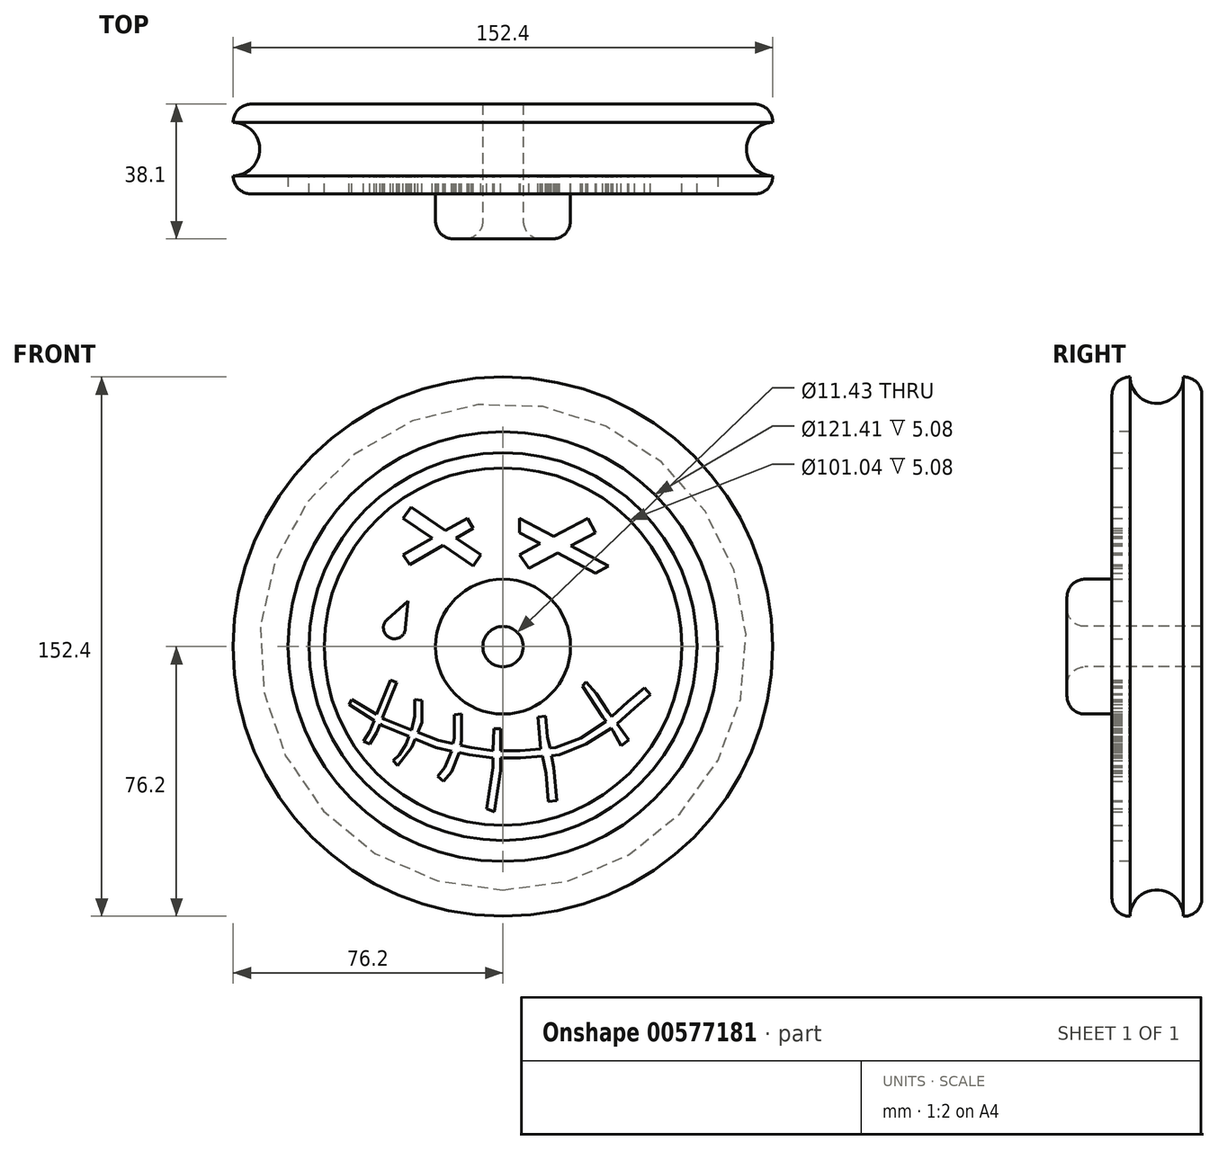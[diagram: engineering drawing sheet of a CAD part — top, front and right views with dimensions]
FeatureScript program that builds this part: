
annotation { "Feature Type Name" : "Feature", "Feature Type Description" : "" }
export const myFeature = defineFeature(function(context is Context, id is Id, definition is map)
    precondition{}
    {
        {
            var Q0;
            Q0=qCreatedBy(makeId("Front.planeOp"),FACE);
            var sketch = newSketch(context, id + "F0", { "sketchPlane" : qUnion([Q0])});
            skCircle(sketch, "E0", {"center": v(0, 0) * mm, "radius": 76.2 * mm});
            skSolve(sketch);
        }
        {
            var Q0;
            Q0=makeQuery(id+"F0.imprint","IMPRINT",FACE,{"disambiguationData":[TD([[makeQuery(id+"F0.imprint","IMPRINT",EDGE,{"derivedFrom":sQuery(id+"F0.wireOp",EDGE,"E0")}),1.0]])]});
            extrude(context, id + "F1", {"entities" : qUnion([Q0]), "depth" : 25.4 * mm, "offsetDistance" : 25.4 * mm, "symmetric" : true});
        }
        {
            var Q0;
            Q0=makeQuery(id+"F1.opExtrude","CAP_FACE",FACE,{"disambiguationData":[OSD([sQuery(id+"F0.wireOp",EDGE,"E0")])],"isStart":false});
            var sketch = newSketch(context, id + "F2", { "sketchPlane" : qUnion([Q0])});
            skCircle(sketch, "E1", {"center": v(0, 0) * mm, "radius": 19.05 * mm});
            skSolve(sketch);
        }
        {
            var Q0;
            Q0=makeQuery(id+"F2.imprint","IMPRINT",FACE,{"disambiguationData":[TD([[makeQuery(id+"F2.imprint","IMPRINT",EDGE,{"derivedFrom":sQuery(id+"F2.wireOp",EDGE,"E1")}),1.0]])]});
            extrude(context, id + "F3", {"entities" : qUnion([Q0]), "operationType" : NewBodyOperationType.ADD, "depth" : 12.7 * mm, "offsetDistance" : 25.4 * mm});
        }
        {
            var Q0;
            Q0=makeQuery(id+"F3.opExtrude","CAP_FACE",FACE,{"disambiguationData":[OSD([sQuery(id+"F2.wireOp",EDGE,"E1")])],"isStart":false});
            var sketch = newSketch(context, id + "F4", { "sketchPlane" : qUnion([Q0])});
            skCircle(sketch, "E2", {"center": v(0, 0) * mm, "radius": 5.72 * mm});
            skSolve(sketch);
        }
        {
            var Q0;
            Q0=sQuery(id+"F4.wireOp",VERTEX,"E2.center");
            var Q1;
            Q1=makeQuery(id+"F1.opExtrude","SWEPT_BODY",BODY,{"disambiguationData":[OSD([sQuery(id+"F0.wireOp",EDGE,"E0")])]});
            hole(context, id + "F5", {"style" : HoleStyle.SIMPLE, "endStyle" : HoleEndStyle.THROUGH, "holeDiameter" : 11.43 * mm, "isTappedThrough" : true, "tappedDepth" : 12.7 * mm, "tapClearance" : 3, "locations" : qUnion([Q0]), "scope" : qUnion([Q1])});
        }
        {
            var Q0;
            Q0=makeQuery(id+"F1.opExtrude","CAP_EDGE",EDGE,{"disambiguationData":[OSD([sQuery(id+"F0.wireOp",EDGE,"E0")])],"isStart":false});
            var Q1;
            Q1=makeQuery(id+"F1.opExtrude","SWEPT_FACE",FACE,{"disambiguationData":[OSD([sQuery(id+"F0.wireOp",EDGE,"E0")])]});
            var Q2;
            Q2=makeQuery(id+"F3.opExtrude","CAP_FACE",FACE,{"disambiguationData":[OSD([sQuery(id+"F2.wireOp",EDGE,"E1")])],"isStart":false});
            fillet(context, id + "F6", {"entities" : qUnion([Q0, Q1, Q2]), "radius" : 5.08 * mm, "tangentPropagation" : true, "allowEdgeOverflow" : false});
        }
        {
            var Q0;
            Q0=makeQuery(id+"F1.opExtrude","CAP_FACE",FACE,{"disambiguationData":[OSD([sQuery(id+"F0.wireOp",EDGE,"E0")])],"isStart":false});
            var sketch = newSketch(context, id + "F7", { "sketchPlane" : qUnion([Q0])});
            skCircle(sketch, "E3", {"center": v(0, 0) * mm, "radius": 60.7 * mm});
            skSolve(sketch);
        }
        {
            var Q0;
            Q0=makeQuery(id+"F7.imprint","IMPRINT",FACE,{"disambiguationData":[TD([[makeQuery(id+"F7.imprint","IMPRINT",EDGE,{"derivedFrom":sQuery(id+"F7.wireOp",EDGE,"E3")}),1.0]])]});
            extrude(context, id + "F8", {"entities" : qUnion([Q0]), "operationType" : NewBodyOperationType.REMOVE, "oppositeDirection" : true, "depth" : 5.08 * mm, "offsetDistance" : 25.4 * mm});
        }
        {
            var Q0;
            Q0=makeQuery(id+"F8.boolean.opBoolean","COPY",FACE,{"derivedFrom":makeQuery(id+"F8.opExtrude","CAP_FACE",FACE,{"disambiguationData":[OSD([sQuery(id+"F2.wireOp",EDGE,"E1"),sQuery(id+"F7.wireOp",EDGE,"E3")])],"isStart":false})});
            var sketch = newSketch(context, id + "F9", { "sketchPlane" : qUnion([Q0])});
            skCircle(sketch, "E4", {"center": v(0, 0) * mm, "radius": 54.78 * mm});
            skCircle(sketch, "E5", {"center": v(0, 0) * mm, "radius": 50.52 * mm});
            skSolve(sketch);
        }
        {
            var Q0;
            Q0=makeQuery(id+"F9.imprint","IMPRINT",FACE,{"disambiguationData":[TD([[makeQuery(id+"F9.imprint","IMPRINT",EDGE,{"derivedFrom":sQuery(id+"F9.wireOp",EDGE,"E5")}),1.0]])]});
            var sketch = newSketch(context, id + "F10", { "sketchPlane" : qUnion([Q0])});
            skLineSegment(sketch, "E6", {"start": v(-28.19, 25.94) * mm, "end": v(-10.05, 36.3) * mm});
            skLineSegment(sketch, "E7", {"start": v(-10.05, 36.3) * mm, "end": v(-8.42, 33.43) * mm});
            skLineSegment(sketch, "E8", {"start": v(-8.42, 33.43) * mm, "end": v(-26.29, 23.22) * mm});
            skLineSegment(sketch, "E9", {"start": v(-26.29, 23.22) * mm, "end": v(-28.19, 25.94) * mm});
            skLineSegment(sketch, "E10", {"start": v(-28.19, 36.3) * mm, "end": v(-8.42, 22.78) * mm});
            skLineSegment(sketch, "E11", {"start": v(-8.42, 22.78) * mm, "end": v(-6.26, 25.94) * mm});
            skLineSegment(sketch, "E12", {"start": v(-6.26, 25.94) * mm, "end": v(-25.93, 39.4) * mm});
            skLineSegment(sketch, "E13", {"start": v(-25.93, 39.4) * mm, "end": v(-28.19, 36.3) * mm});
            skLineSegment(sketch, "E14", {"start": v(4.65, 25.95) * mm, "end": v(23.96, 36.3) * mm});
            skLineSegment(sketch, "E15", {"start": v(23.96, 36.3) * mm, "end": v(26.15, 32.23) * mm});
            skLineSegment(sketch, "E16", {"start": v(26.15, 32.23) * mm, "end": v(7.28, 22.12) * mm});
            skLineSegment(sketch, "E17", {"start": v(7.28, 22.12) * mm, "end": v(4.65, 25.95) * mm});
            skLineSegment(sketch, "E18", {"start": v(4.65, 36.3) * mm, "end": v(29.75, 22.73) * mm});
            skLineSegment(sketch, "E19", {"start": v(29.75, 22.73) * mm, "end": v(26.15, 20.8) * mm});
            skLineSegment(sketch, "E20", {"start": v(26.15, 20.8) * mm, "end": v(4.65, 32.23) * mm});
            skLineSegment(sketch, "E21", {"start": v(4.65, 32.23) * mm, "end": v(4.65, 36.3) * mm});
            skSolve(sketch);
        }
        {
            var Q0;
            Q0 = qSketchRegion(id + "F10", true);
            extrude(context, id + "F11", {"entities" : qUnion([Q0]), "operationType" : NewBodyOperationType.ADD, "depth" : 5.08 * mm, "offsetDistance" : 25.4 * mm});
        }
        {
            var Q0;
            Q0=makeQuery(id+"F9.imprint","IMPRINT",FACE,{"disambiguationData":[TD([[makeQuery(id+"F9.imprint","IMPRINT",EDGE,{"derivedFrom":sQuery(id+"F9.wireOp",EDGE,"E4")}),1.0]])]});
            extrude(context, id + "F12", {"entities" : qUnion([Q0]), "operationType" : NewBodyOperationType.ADD, "depth" : 5.08 * mm, "offsetDistance" : 25.4 * mm});
        }
        {
            var Q0;
            {var subQ4=sQuery(id+"F2.wireOp",EDGE,"E1");Q0=makeQuery(id+"F12.boolean.opBoolean","SPLIT",FACE,{"disambiguationData":[TD([makeQuery(id+"F3.opExtrude","SWEPT_FACE",FACE,{"disambiguationData":[OSD([subQ4])]})])],"derivedFrom":makeQuery(id+"F8.boolean.opBoolean","COPY",FACE,{"derivedFrom":makeQuery(id+"F8.opExtrude","CAP_FACE",FACE,{"disambiguationData":[OSD([subQ4,sQuery(id+"F7.wireOp",EDGE,"E3")])],"isStart":false})})});}
            var sketch = newSketch(context, id + "F13", { "sketchPlane" : qUnion([Q0])});
            skLineSegment(sketch, "E22", {"start": v(-42.77, -14.96) * mm, "end": v(-33.4, -20.53) * mm});
            skLineSegment(sketch, "E23", {"start": v(-33.4, -20.53) * mm, "end": v(-18.23, -26.56) * mm});
            skLineSegment(sketch, "E24", {"start": v(-18.23, -26.56) * mm, "end": v(-8.86, -28.57) * mm});
            skLineSegment(sketch, "E25", {"start": v(-8.86, -28.57) * mm, "end": v(-2.84, -29.46) * mm});
            skLineSegment(sketch, "E26", {"start": v(-2.84, -29.46) * mm, "end": v(4.75, -29.46) * mm});
            skLineSegment(sketch, "E27", {"start": v(4.75, -29.46) * mm, "end": v(14.79, -28.57) * mm});
            skLineSegment(sketch, "E28", {"start": v(14.79, -28.57) * mm, "end": v(21.92, -25.89) * mm});
            skLineSegment(sketch, "E29", {"start": v(21.92, -25.89) * mm, "end": v(29.06, -21.2) * mm});
            skLineSegment(sketch, "E30", {"start": v(29.06, -21.2) * mm, "end": v(35.31, -15.63) * mm});
            skLineSegment(sketch, "E31", {"start": v(35.31, -15.63) * mm, "end": v(40, -11.61) * mm});
            skLineSegment(sketch, "E32", {"start": v(40, -11.61) * mm, "end": v(41.62, -13.5) * mm});
            skLineSegment(sketch, "E33", {"start": v(41.62, -13.5) * mm, "end": v(37.12, -17.36) * mm});
            skLineSegment(sketch, "E34", {"start": v(37.12, -17.36) * mm, "end": v(31.07, -22.76) * mm});
            skLineSegment(sketch, "E35", {"start": v(31.07, -22.76) * mm, "end": v(23.49, -27.45) * mm});
            skLineSegment(sketch, "E36", {"start": v(23.49, -27.45) * mm, "end": v(15.9, -30.57) * mm});
            skLineSegment(sketch, "E37", {"start": v(15.9, -30.57) * mm, "end": v(4.97, -31.47) * mm});
            skLineSegment(sketch, "E38", {"start": v(4.97, -31.47) * mm, "end": v(-2.4, -31.47) * mm});
            skLineSegment(sketch, "E39", {"start": v(-2.4, -31.47) * mm, "end": v(-9.53, -30.57) * mm});
            skLineSegment(sketch, "E40", {"start": v(-9.53, -30.57) * mm, "end": v(-18.9, -28.57) * mm});
            skLineSegment(sketch, "E41", {"start": v(-18.9, -28.57) * mm, "end": v(-34.07, -22.32) * mm});
            skLineSegment(sketch, "E42", {"start": v(-34.07, -22.32) * mm, "end": v(-43.44, -16.3) * mm});
            skLineSegment(sketch, "E43", {"start": v(-43.44, -16.3) * mm, "end": v(-42.77, -14.96) * mm});
            skLineSegment(sketch, "E44", {"start": v(-30.05, -10.05) * mm, "end": v(-35.74, -24.37) * mm});
            skLineSegment(sketch, "E45", {"start": v(-35.74, -24.37) * mm, "end": v(-37.57, -27.45) * mm});
            skLineSegment(sketch, "E46", {"start": v(-37.57, -27.45) * mm, "end": v(-39.36, -26.74) * mm});
            skLineSegment(sketch, "E47", {"start": v(-39.36, -26.74) * mm, "end": v(-37.57, -23.96) * mm});
            skLineSegment(sketch, "E48", {"start": v(-37.57, -23.96) * mm, "end": v(-31.82, -9.47) * mm});
            skLineSegment(sketch, "E49", {"start": v(-31.82, -9.47) * mm, "end": v(-30.05, -10.05) * mm});
            skLineSegment(sketch, "E50", {"start": v(-24.92, -14.96) * mm, "end": v(-24.92, -17.36) * mm});
            skLineSegment(sketch, "E51", {"start": v(-24.92, -17.36) * mm, "end": v(-24.92, -19.64) * mm});
            skLineSegment(sketch, "E52", {"start": v(-24.92, -19.64) * mm, "end": v(-25.82, -23.55) * mm});
            skLineSegment(sketch, "E53", {"start": v(-25.82, -23.55) * mm, "end": v(-27.37, -27.45) * mm});
            skLineSegment(sketch, "E54", {"start": v(-27.37, -27.45) * mm, "end": v(-29.23, -30.57) * mm});
            skLineSegment(sketch, "E55", {"start": v(-29.23, -30.57) * mm, "end": v(-31.08, -32.23) * mm});
            skLineSegment(sketch, "E56", {"start": v(-31.08, -32.23) * mm, "end": v(-29.81, -33.66) * mm});
            skLineSegment(sketch, "E57", {"start": v(-29.81, -33.66) * mm, "end": v(-25.82, -28.57) * mm});
            skLineSegment(sketch, "E58", {"start": v(-25.82, -28.57) * mm, "end": v(-24.81, -26.13) * mm});
            skLineSegment(sketch, "E59", {"start": v(-24.81, -26.13) * mm, "end": v(-24.06, -24.24) * mm});
            skLineSegment(sketch, "E60", {"start": v(-24.06, -24.24) * mm, "end": v(-22.96, -21.45) * mm});
            skLineSegment(sketch, "E61", {"start": v(-22.96, -21.45) * mm, "end": v(-22.96, -18.3) * mm});
            skLineSegment(sketch, "E62", {"start": v(-22.96, -18.3) * mm, "end": v(-22.96, -15.18) * mm});
            skLineSegment(sketch, "E63", {"start": v(-22.96, -15.18) * mm, "end": v(-24.92, -14.96) * mm});
            skLineSegment(sketch, "E64", {"start": v(-13.77, -19.2) * mm, "end": v(-13.77, -23.66) * mm});
            skLineSegment(sketch, "E65", {"start": v(-13.77, -23.66) * mm, "end": v(-13.77, -25.89) * mm});
            skLineSegment(sketch, "E66", {"start": v(-13.77, -25.89) * mm, "end": v(-14.54, -29.5) * mm});
            skLineSegment(sketch, "E67", {"start": v(-14.54, -29.5) * mm, "end": v(-16.38, -34.12) * mm});
            skLineSegment(sketch, "E68", {"start": v(-16.38, -34.12) * mm, "end": v(-18.45, -36.6) * mm});
            skLineSegment(sketch, "E69", {"start": v(-18.45, -36.6) * mm, "end": v(-16.77, -38.01) * mm});
            skLineSegment(sketch, "E70", {"start": v(-16.77, -38.01) * mm, "end": v(-14.58, -35.4) * mm});
            skLineSegment(sketch, "E71", {"start": v(-14.58, -35.4) * mm, "end": v(-12.42, -29.95) * mm});
            skLineSegment(sketch, "E72", {"start": v(-12.42, -29.95) * mm, "end": v(-11.69, -26.56) * mm});
            skLineSegment(sketch, "E73", {"start": v(-11.69, -26.56) * mm, "end": v(-11.69, -22.54) * mm});
            skLineSegment(sketch, "E74", {"start": v(-11.69, -22.54) * mm, "end": v(-11.69, -18.97) * mm});
            skLineSegment(sketch, "E75", {"start": v(-11.69, -18.97) * mm, "end": v(-13.77, -19.2) * mm});
            skLineSegment(sketch, "E76", {"start": v(-2.61, -23.21) * mm, "end": v(-2.84, -29.46) * mm});
            skLineSegment(sketch, "E77", {"start": v(-2.84, -34.12) * mm, "end": v(-2.84, -29.46) * mm});
            skLineSegment(sketch, "E78", {"start": v(-2.84, -34.12) * mm, "end": v(-3.7, -39.98) * mm});
            skLineSegment(sketch, "E79", {"start": v(-3.7, -39.98) * mm, "end": v(-4.57, -45.82) * mm});
            skLineSegment(sketch, "E80", {"start": v(-4.57, -45.82) * mm, "end": v(-2.4, -46.68) * mm});
            skLineSegment(sketch, "E81", {"start": v(-2.4, -46.68) * mm, "end": v(-1.5, -40.61) * mm});
            skLineSegment(sketch, "E82", {"start": v(-1.5, -40.61) * mm, "end": v(-0.66, -35.03) * mm});
            skLineSegment(sketch, "E83", {"start": v(-0.66, -35.03) * mm, "end": v(-0.66, -31.47) * mm});
            skLineSegment(sketch, "E84", {"start": v(-0.66, -31.47) * mm, "end": v(-0.66, -26.56) * mm});
            skLineSegment(sketch, "E85", {"start": v(-0.66, -26.56) * mm, "end": v(-0.66, -23.21) * mm});
            skLineSegment(sketch, "E86", {"start": v(9.88, -19.86) * mm, "end": v(10.68, -28.93) * mm});
            skLineSegment(sketch, "E87", {"start": v(10.68, -28.93) * mm, "end": v(12.1, -35.7) * mm});
            skLineSegment(sketch, "E88", {"start": v(12.1, -35.7) * mm, "end": v(12.59, -41.07) * mm});
            skLineSegment(sketch, "E89", {"start": v(12.59, -41.07) * mm, "end": v(12.83, -43.77) * mm});
            skLineSegment(sketch, "E90", {"start": v(12.83, -43.77) * mm, "end": v(15.2, -43.56) * mm});
            skLineSegment(sketch, "E91", {"start": v(15.2, -43.56) * mm, "end": v(14.52, -35.9) * mm});
            skLineSegment(sketch, "E92", {"start": v(14.52, -35.9) * mm, "end": v(14.36, -34.1) * mm});
            skLineSegment(sketch, "E93", {"start": v(14.36, -34.1) * mm, "end": v(12.56, -25.44) * mm});
            skLineSegment(sketch, "E94", {"start": v(12.56, -25.44) * mm, "end": v(12.04, -19.64) * mm});
            skLineSegment(sketch, "E95", {"start": v(12.04, -19.64) * mm, "end": v(9.88, -19.86) * mm});
            skLineSegment(sketch, "E96", {"start": v(22.46, -11.18) * mm, "end": v(28.17, -19.86) * mm});
            skLineSegment(sketch, "E97", {"start": v(33.36, -28) * mm, "end": v(35.58, -26.35) * mm});
            skLineSegment(sketch, "E98", {"start": v(35.58, -26.35) * mm, "end": v(29.73, -18.41) * mm});
            skPoint(sketch, "E98.endSnap0", {"position": v(32.19, -18.41) * mm});
            skLineSegment(sketch, "E99", {"start": v(29.73, -18.41) * mm, "end": v(26.35, -13.27) * mm});
            skLineSegment(sketch, "E100", {"start": v(26.35, -13.27) * mm, "end": v(23.45, -10.02) * mm});
            skLineSegment(sketch, "E101", {"start": v(23.45, -10.02) * mm, "end": v(22.46, -11.18) * mm});
            skLineSegment(sketch, "E102", {"start": v(28.17, -19.86) * mm, "end": v(31.07, -23.8) * mm});
            skLineSegment(sketch, "E103", {"start": v(31.07, -23.8) * mm, "end": v(33.36, -28) * mm});
            skLineSegment(sketch, "E104", {"start": v(-2.61, -23.21) * mm, "end": v(-0.66, -23.21) * mm});
            skSolve(sketch);
        }
        {
            var Q0;
            Q0 = qSketchRegion(id + "F13", true);
            extrude(context, id + "F14", {"entities" : qUnion([Q0]), "operationType" : NewBodyOperationType.ADD, "depth" : 5.08 * mm, "offsetDistance" : 25.4 * mm});
        }
        {
            var Q0;
            {var subQ4=sQuery(id+"F2.wireOp",EDGE,"E1");Q0=makeQuery(id+"F12.boolean.opBoolean","SPLIT",FACE,{"disambiguationData":[TD([makeQuery(id+"F3.opExtrude","SWEPT_FACE",FACE,{"disambiguationData":[OSD([subQ4])]})])],"derivedFrom":makeQuery(id+"F8.boolean.opBoolean","COPY",FACE,{"derivedFrom":makeQuery(id+"F8.opExtrude","CAP_FACE",FACE,{"disambiguationData":[OSD([subQ4,sQuery(id+"F7.wireOp",EDGE,"E3")])],"isStart":false})})});}
            var sketch = newSketch(context, id + "F15", { "sketchPlane" : qUnion([Q0])});
            skCircle(sketch, "E105", {"center": v(-30.65, 5.34) * mm, "radius": 3.13 * mm});
            skLineSegment(sketch, "E106", {"start": v(-32.73, 7.68) * mm, "end": v(-26.88, 12.89) * mm});
            skLineSegment(sketch, "E107", {"start": v(-26.88, 12.89) * mm, "end": v(-27.54, 5.08) * mm});
            skSolve(sketch);
        }
        {
            var Q0;
            Q0 = qSketchRegion(id + "F15", true);
            extrude(context, id + "F16", {"entities" : qUnion([Q0]), "operationType" : NewBodyOperationType.ADD, "depth" : 5.08 * mm, "offsetDistance" : 25.4 * mm});
        }
        {
            var Q0;
            Q0=qCreatedBy(makeId("Right.planeOp"),FACE);
            var sketch = newSketch(context, id + "F17", { "sketchPlane" : qUnion([Q0])});
            skCircle(sketch, "E108", {"center": v(-0.05, 76.27) * mm, "radius": 7.54 * mm});
            skPoint(sketch, "E108.first.point", {"position": v(-7.58, 76.4) * mm});
            skPoint(sketch, "E108.second.point", {"position": v(7.49, 76.31) * mm});
            skPoint(sketch, "E108.third.point", {"position": v(0, 68.73) * mm});
            skSolve(sketch);
        }
        {
            var Q0;
            Q0=makeQuery(id+"F17.imprint","IMPRINT",FACE,{"disambiguationData":[TD([[makeQuery(id+"F17.imprint","IMPRINT",EDGE,{"derivedFrom":sQuery(id+"F17.wireOp",EDGE,"E108")}),1.0]])]});
            var Q1;
            {var subQ0=sQuery(id+"F0.wireOp",EDGE,"E0");Q1=makeQuery(id+"F6.opFillet","BLEND_EDGE",EDGE,{"blendedFrom":[makeQuery(id+"F1.opExtrude","CAP_EDGE",EDGE,{"disambiguationData":[OSD([subQ0])],"isStart":true}),makeQuery(id+"F1.opExtrude","CAP_FACE",FACE,{"disambiguationData":[OSD([subQ0])],"isStart":true})],"blendedInto":[makeQuery(id+"F1.opExtrude","CAP_FACE",FACE,{"disambiguationData":[OSD([subQ0])],"isStart":true})]});}
            revolve(context, id + "F18", {"operationType" : NewBodyOperationType.REMOVE, "entities" : qUnion([Q0]), "axis" : qUnion([Q1]), "revolveType" : RevolveType.FULL, "oppositeDirection" : true});
        }
    });
